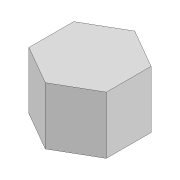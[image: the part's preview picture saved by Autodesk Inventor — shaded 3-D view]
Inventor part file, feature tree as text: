
AUTODESK INVENTOR PART (.ipt)
format: ipt  version: 2022 (Build 260153000, 153)  size: 77,312 bytes
history: native  units: mm
features: extrude x1, sketch x1
ambient origin geometry x8: Origin, YZ Plane, XZ Plane, XY Plane, X Axis, Y Axis, Z Axis, Center Point
bodies: Solid1 (feature_tree)
feature tree (2):
  extrude  "Extrusion1"  Depth=4.0mm TaperAngle=0.0deg
  sketch  "Sketch1"  dims[d0=5.4mm d1=4.0mm d2=0.0mm]
